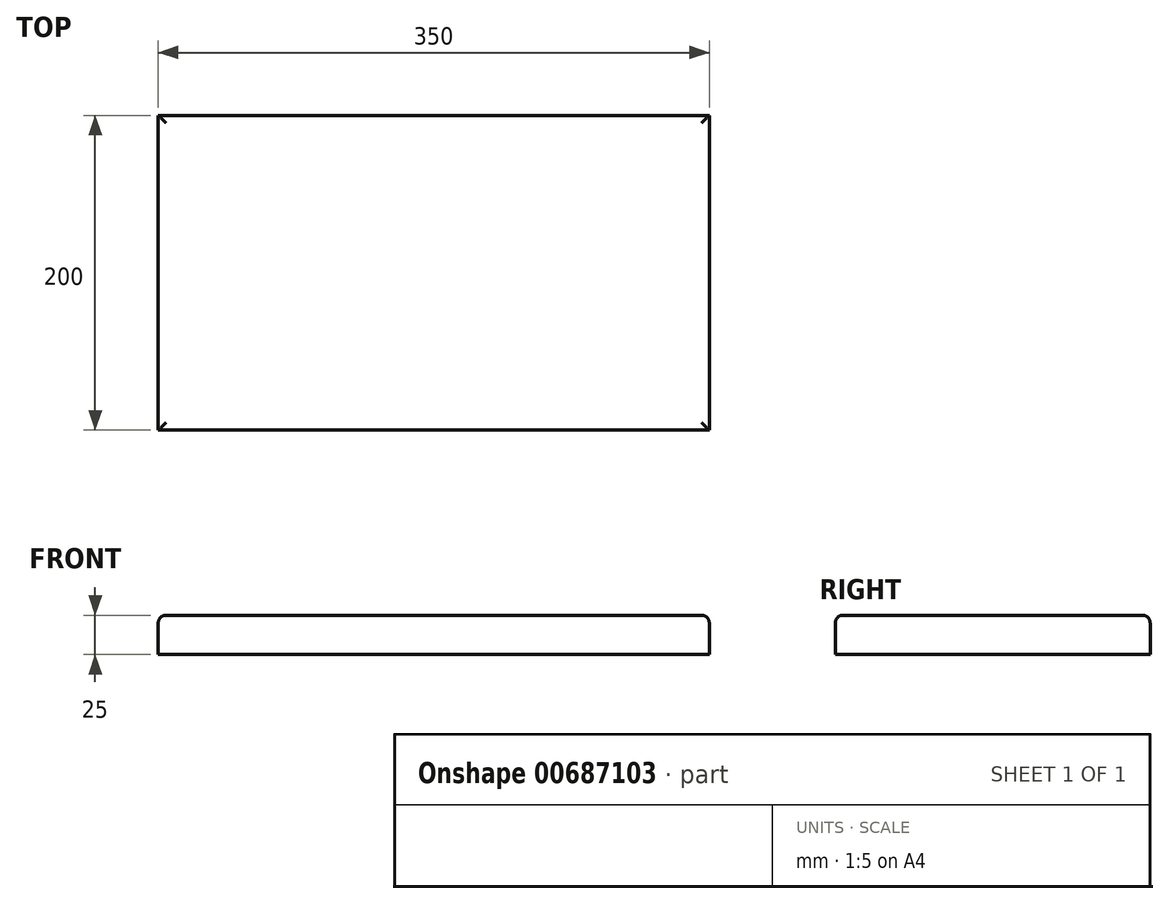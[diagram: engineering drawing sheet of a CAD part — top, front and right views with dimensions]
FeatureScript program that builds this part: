
annotation { "Feature Type Name" : "Feature", "Feature Type Description" : "" }
export const myFeature = defineFeature(function(context is Context, id is Id, definition is map)
    precondition{}
    {
        {
            var Q0;
            Q0=qCreatedBy(makeId("Top.planeOp"),FACE);
            var sketch = newSketch(context, id + "F0", { "sketchPlane" : qUnion([Q0])});
            skLineSegment(sketch, "E0.bottom", {"start": v(-235.3, 112.72) * mm, "end": v(114.7, 112.72) * mm});
            skLineSegment(sketch, "E0.top", {"start": v(-235.3, -87.28) * mm, "end": v(114.7, -87.28) * mm});
            skLineSegment(sketch, "E0.left", {"start": v(-235.3, 112.72) * mm, "end": v(-235.3, -87.28) * mm});
            skLineSegment(sketch, "E0.right", {"start": v(114.7, 112.72) * mm, "end": v(114.7, -87.28) * mm});
            skSolve(sketch);
        }
        {
            var Q0;
            Q0=makeQuery(id+"F0.imprint","IMPRINT",FACE,{"disambiguationData":[TD([[makeQuery(id+"F0.imprint","IMPRINT",EDGE,{"derivedFrom":sQuery(id+"F0.wireOp",EDGE,"E0.bottom")}),-1.0]])]});
            extrude(context, id + "F1", {"entities" : qUnion([Q0]), "depth" : 25 * mm, "offsetDistance" : 25 * mm});
        }
        {
            var Q0;
            Q0=makeQuery(id+"F1.opExtrude","CAP_FACE",FACE,{"disambiguationData":[OSD([sQuery(id+"F0.wireOp",EDGE,"E0.bottom"),sQuery(id+"F0.wireOp",EDGE,"E0.top"),sQuery(id+"F0.wireOp",EDGE,"E0.left"),sQuery(id+"F0.wireOp",EDGE,"E0.right")])],"isStart":false});
            var Q1;
            Q1=makeQuery(id+"F1.opExtrude","CAP_EDGE",EDGE,{"disambiguationData":[OSD([sQuery(id+"F0.wireOp",EDGE,"E0.top")])],"isStart":false});
            fillet(context, id + "F2", {"entities" : qUnion([Q0, Q1]), "radius" : 5 * mm, "tangentPropagation" : true, "allowEdgeOverflow" : false});
        }
    });
